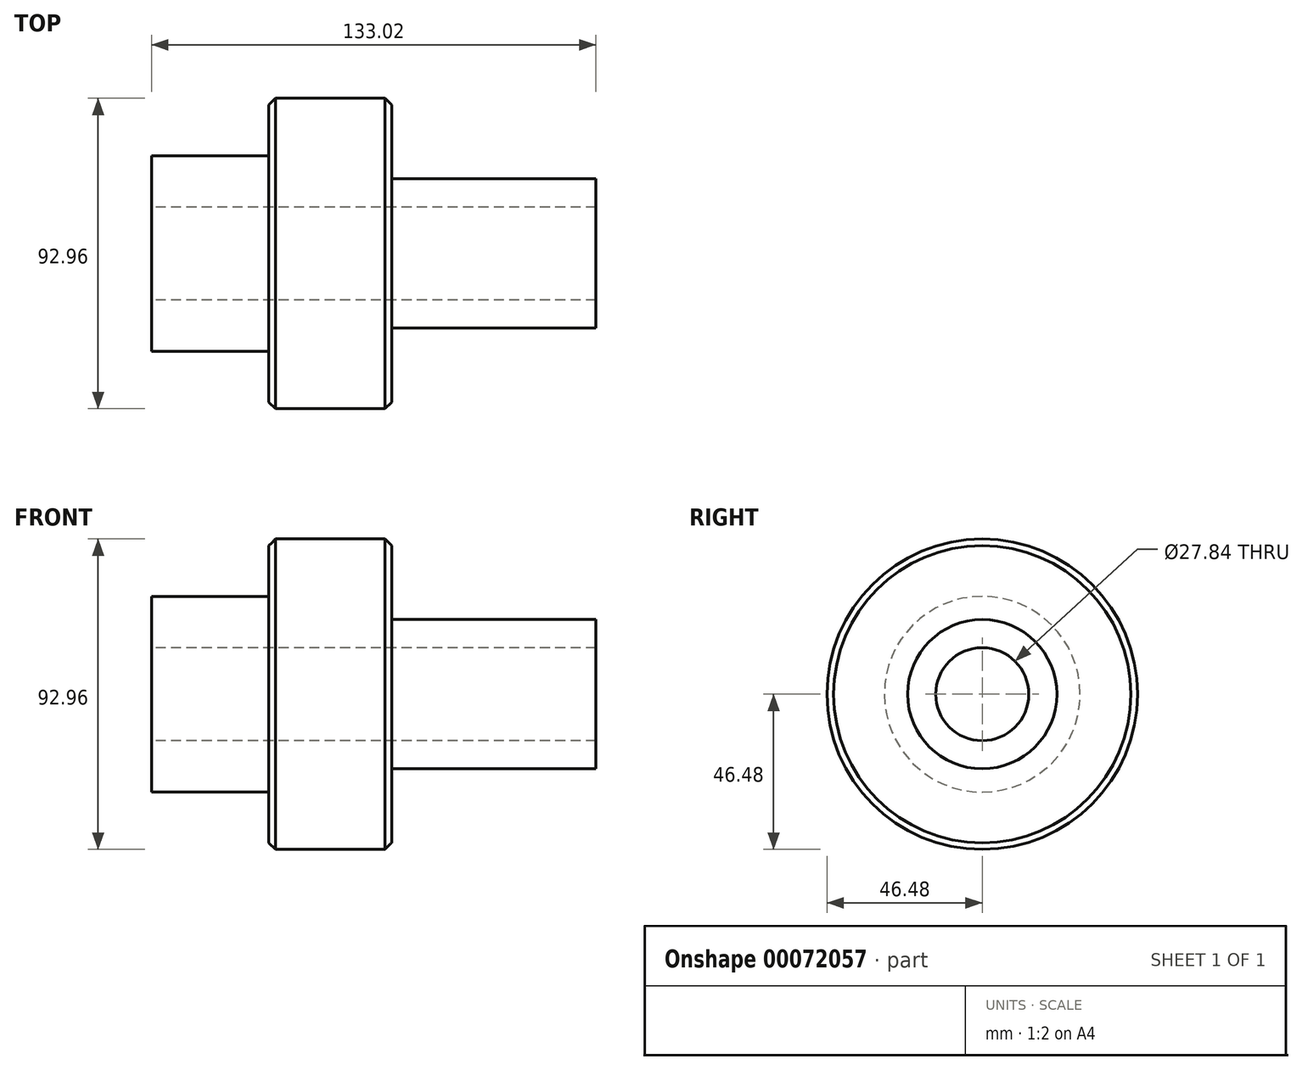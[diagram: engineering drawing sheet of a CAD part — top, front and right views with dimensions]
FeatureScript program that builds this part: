
annotation { "Feature Type Name" : "Feature", "Feature Type Description" : "" }
export const myFeature = defineFeature(function(context is Context, id is Id, definition is map)
    precondition{}
    {
        {
            var Q0;
            Q0=qCreatedBy(makeId("Front.planeOp"),FACE);
            var sketch = newSketch(context, id + "F0", { "sketchPlane" : qUnion([Q0])});
            skLineSegment(sketch, "E0", {"start": v(0, 13.92) * mm, "end": v(0, 29.3) * mm});
            skLineSegment(sketch, "E1", {"start": v(0, 29.3) * mm, "end": v(35.1, 29.3) * mm});
            skLineSegment(sketch, "E2", {"start": v(35.1, 29.3) * mm, "end": v(35.1, 46.48) * mm});
            skLineSegment(sketch, "E3", {"start": v(35.1, 46.48) * mm, "end": v(71.82, 46.48) * mm});
            skLineSegment(sketch, "E4", {"start": v(71.82, 46.48) * mm, "end": v(71.82, 22.34) * mm});
            skLineSegment(sketch, "E5", {"start": v(71.82, 22.34) * mm, "end": v(133.02, 22.34) * mm});
            skLineSegment(sketch, "E6", {"start": v(133.02, 22.34) * mm, "end": v(133.02, 13.92) * mm});
            skLineSegment(sketch, "E7", {"start": v(133.02, 13.92) * mm, "end": v(0, 13.92) * mm});
            skLineSegment(sketch, "E8", {"start": v(0, 0) * mm, "end": v(136.38, 0) * mm});
            skSolve(sketch);
        }
        {
            var Q0;
            Q0=makeQuery(id+"F0.imprint","IMPRINT",FACE,{"disambiguationData":[TD([[makeQuery(id+"F0.imprint","IMPRINT",EDGE,{"derivedFrom":sQuery(id+"F0.wireOp",EDGE,"E0")}),-1.0]])]});
            var Q1;
            Q1=sQuery(id+"F0.wireOp",EDGE,"E8");
            revolve(context, id + "F1", {"entities" : qUnion([Q0]), "axis" : qUnion([Q1]), "revolveType" : RevolveType.FULL});
        }
        {
            var Q0;
            Q0=makeQuery(id+"F1.opRevolve","SWEPT_EDGE",EDGE,{"disambiguationData":[OSD([sQuery(id+"F0.wireOp",EDGE,"E3"),sQuery(id+"F0.wireOp",EDGE,"E4")])]});
            var Q1;
            Q1=makeQuery(id+"F1.opRevolve","SWEPT_EDGE",EDGE,{"disambiguationData":[OSD([sQuery(id+"F0.wireOp",EDGE,"E2"),sQuery(id+"F0.wireOp",EDGE,"E3")])]});
            chamfer(context, id + "F2", {"entities" : qUnion([Q0, Q1]), "width" : 2 * mm, "tangentPropagation" : true});
        }
    });
